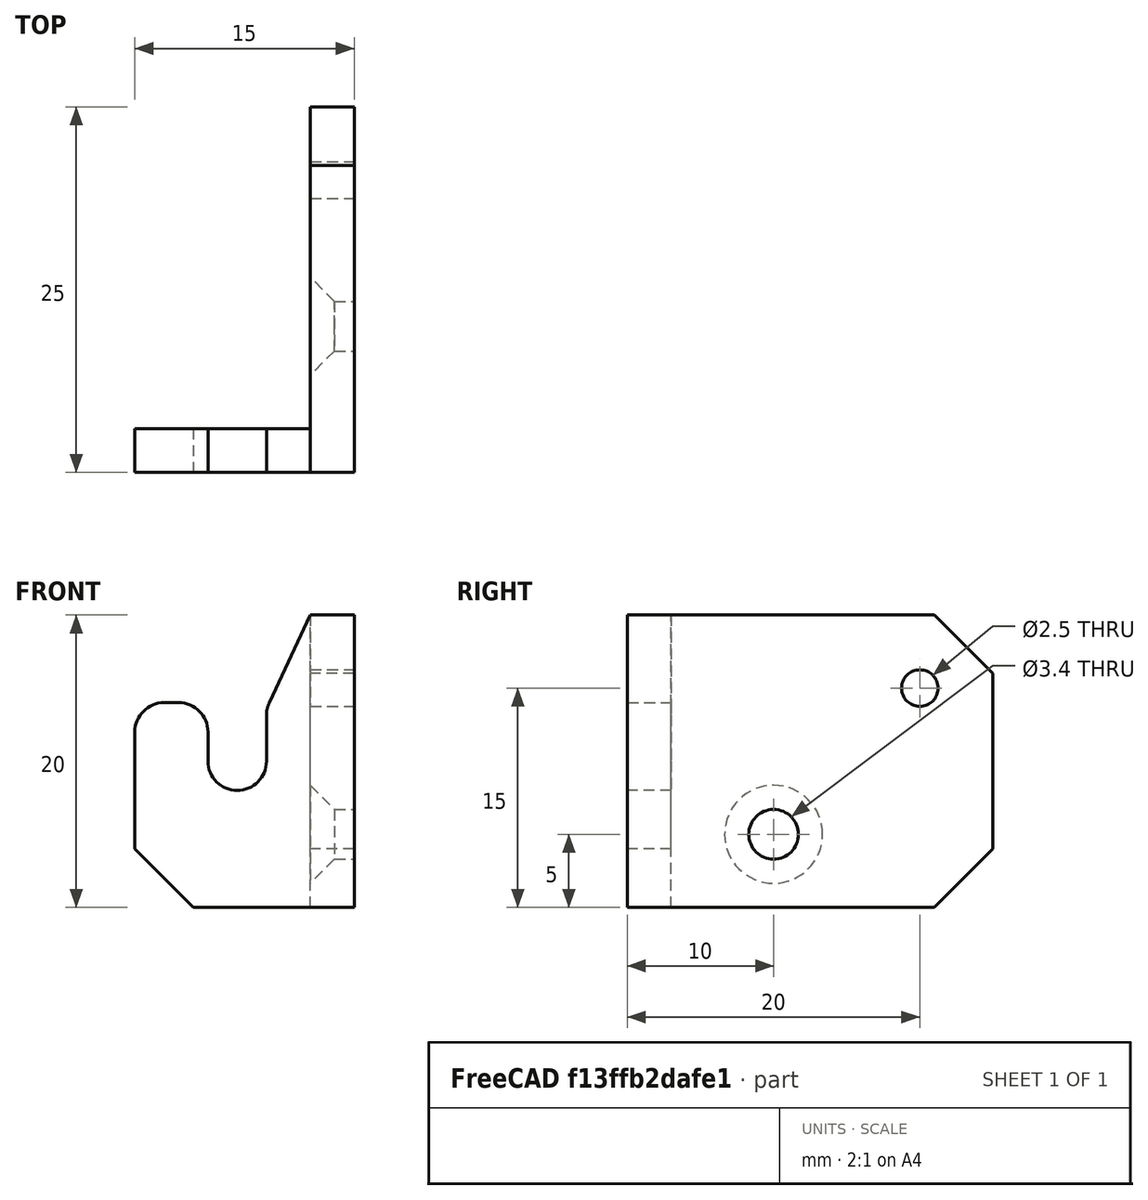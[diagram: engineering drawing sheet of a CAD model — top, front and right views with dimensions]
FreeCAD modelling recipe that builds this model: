
FCSTD DOCUMENT  (FreeCAD 0.20R28730 (Git))
Label: Tip Remover Bracket
License: All rights reserved
LicenseURL: http://en.wikipedia.org/wiki/All_rights_reserved
objects: TechDraw::DrawViewDimension×14, Sketcher::SketchObject×4, PartDesign::CoordinateSystem×4, TechDraw::DrawProjGroupItem×4, TechDraw::DrawViewBalloon×4, PartDesign::Hole×2, PartDesign::Pad×1, PartDesign::Pocket×1, PartDesign::Chamfer×1, TechDraw::DrawSVGTemplate×1, PartDesign::Body×1, TechDraw::DrawProjGroup×1, TechDraw::DrawViewAnnotation×1, TechDraw::DrawPage×1
note: 19 computed .brp shape members not serialized (recipe doc carries the construction recipe); baked Part::Feature solids carry a one-line shape summary decoded from their .brp

FEATURE [Sketcher::SketchObject] Sketch
  FullyConstrained = true
  MapMode = 5
  Support = -> [XY_Plane]
  sketch-geometry (6):
    g0: LineSegment StartX=0 StartY=0 StartZ=0 EndX=0 EndY=25 EndZ=0
    g1: LineSegment StartX=0 StartY=25 StartZ=0 EndX=-3 EndY=25 EndZ=0
    g2: LineSegment StartX=-3 StartY=25 StartZ=0 EndX=-3 EndY=3 EndZ=0
    g3: LineSegment StartX=-3 StartY=3 StartZ=0 EndX=-15 EndY=3 EndZ=0
    g4: LineSegment StartX=-15 StartY=3 StartZ=0 EndX=-15 EndY=0 EndZ=0
    g5: LineSegment StartX=-15 StartY=0 StartZ=0 EndX=0 EndY=0 EndZ=0
  constraints (17):
    c: Coincident(g-1,g0)
    c: PointOnObject(g0,g-2)
    c: Coincident(g0,g1)
    c: Horizontal(g1)
    c: Coincident(g1,g2)
    c: Vertical(g2)
    c: Coincident(g2,g3)
    c: Horizontal(g3)
    c: Coincident(g3,g4)
    c: PointOnObject(g4,g-1)
    c: Vertical(g4)
    c: Coincident(g4,g5)
    c: Coincident(g5,g0)
    c: Equal(g4,g1)
    c: DistanceY(g4,g4) = 3
    c: DistanceY(g0,g0) = 25
    c: DistanceX(g5,g5) = 15
FEATURE [PartDesign::Pad] Pad
  Direction = (0,0,1)
  Length = 20
  Length2 = 10
  Profile = -> Sketch
  ReferenceAxis = -> Sketch [N_Axis]
  Refine = true
  Type = 0
FEATURE [Sketcher::SketchObject] Sketch027
  ExternalGeometry = -> [Pad]
  FullyConstrained = true
  MapMode = 5
  Placement = pos=(0,0,0) rot=(1,0,0;1.5708rad)
  Support = -> [XZ_Plane]
  sketch-geometry (10):
    g0: LineSegment StartX=-3 StartY=20 StartZ=0 EndX=-5.81108 EndY=14 EndZ=0
    g1: LineSegment StartX=-6 StartY=13.1515 StartZ=0 EndX=-6 EndY=10 EndZ=0
    g2: ArcOfCircle CenterX=-8 CenterY=10 CenterZ=0 NormalX=0 NormalY=0 NormalZ=1 AngleXU=0 Radius=2 StartAngle=3.14159 EndAngle=6.28319
    g3: LineSegment StartX=-10 StartY=10 StartZ=0 EndX=-10 EndY=12 EndZ=0
    g4: LineSegment StartX=-15 StartY=12 StartZ=0 EndX=-15 EndY=20 EndZ=0
    g5: LineSegment StartX=-15 StartY=20 StartZ=0 EndX=-3 EndY=20 EndZ=0
    g6: ArcOfCircle CenterX=-12 CenterY=12 CenterZ=0 NormalX=0 NormalY=0 NormalZ=1 AngleXU=0 Radius=2 StartAngle=0 EndAngle=1.5708
    g7: ArcOfCircle CenterX=-4 CenterY=13.1515 CenterZ=0 NormalX=0 NormalY=0 NormalZ=1 AngleXU=0 Radius=2 StartAngle=2.70345 EndAngle=3.14159
    g8: LineSegment StartX=-12 StartY=14 StartZ=0 EndX=-13 EndY=14 EndZ=0
    g9: ArcOfCircle CenterX=-13 CenterY=12 CenterZ=0 NormalX=0 NormalY=0 NormalZ=1 AngleXU=0 Radius=2 StartAngle=1.5708 EndAngle=3.14159
  constraints (25):
    c: Coincident(g-3,g0)
    c: Vertical(g1)
    c: Tangent(g1,g2) = 1.5708
    c: Tangent(g2,g3) = 1.5708
    c: Coincident(g4,g-3)
    c: Vertical(g4)
    c: Coincident(g4,g5)
    c: Coincident(g5,g0)
    c: Vertical(g3)
    c: Radius(g2) = 2
    c: DistanceY(g-1,g2) = 10
    c: Tangent(g3,g6) = -1.5708
    c: Tangent(g0,g7) = -1.5708
    c: Tangent(g1,g7) = -1.5708
    c: Horizontal(g8)
    c: Tangent(g8,g9) = -1.5708
    c: Coincident(g4,g9)
    c: Horizontal(g4,g9)
    c: Tangent(g6,g8) = -1.5708
    c: Equal(g9,g6)
    c: Equal(g6,g7)
    c: Radius(g6) = 2
    c: DistanceX(g2,g-1) = 8
    c: DistanceY(g2,g8) = 4
    c: Horizontal(g6,g0)
FEATURE [PartDesign::Pocket] Pocket
  BaseFeature = -> Pad
  Direction = (0,1,2e-16)
  Length = 5
  Length2 = 5
  Profile = -> Sketch027
  ReferenceAxis = -> Sketch027 [N_Axis]
  Refine = true
  Type = 1
FEATURE [Sketcher::SketchObject] Sketch029
  AttachmentOffset = pos=(0,0,-3) rot=(0,0,1;0rad)
  FullyConstrained = true
  MapMode = 5
  Placement = pos=(-3,7e-16,-7e-16) rot=(0.57735,0.57735,0.57735;2.0944rad)
  Support = -> [YZ_Plane]
  expr: Constraints[1] = Sketch028.Constraints[1]
  expr: Constraints[2] = Sketch028.Constraints[2]
  expr: Constraints[3] = Sketch028.Constraints[3]
  expr: Constraints[4] = Sketch028.Constraints[4]
  expr: Constraints[5] = Sketch028.Constraints[5]
  sketch-geometry (2):
    g0: Circle CenterX=20 CenterY=15 CenterZ=0 NormalX=0 NormalY=0 NormalZ=1 AngleXU=0 Radius=1.5
    g1: Circle CenterX=10 CenterY=5 CenterZ=0 NormalX=0 NormalY=0 NormalZ=1 AngleXU=0 Radius=1.5
  constraints (6):
    c: Equal(g1,g0)
    c: Diameter(g0) = 3
    c: DistanceY(g1,g0) = 10
    c: DistanceX(g1,g0) = 10
    c: DistanceX(g-1,g0) = 20
    c: DistanceY(g-1,g0) = 15
FEATURE [Sketcher::SketchObject] Sketch028
  AttachmentOffset = pos=(0,0,-3) rot=(0,0,1;0rad)
  FullyConstrained = true
  MapMode = 5
  Placement = pos=(-3,7e-16,-7e-16) rot=(0.57735,0.57735,0.57735;2.0944rad)
  Support = -> [YZ_Plane]
  sketch-geometry (2):
    g0: Circle CenterX=20 CenterY=15 CenterZ=0 NormalX=0 NormalY=0 NormalZ=1 AngleXU=0 Radius=1.5
    g1: Circle CenterX=10 CenterY=5 CenterZ=0 NormalX=0 NormalY=0 NormalZ=1 AngleXU=0 Radius=1.5
  constraints (6):
    c: Equal(g1,g0)
    c: Diameter(g0) = 3
    c: DistanceY(g1,g0) = 10
    c: DistanceX(g1,g0) = 10
    c: DistanceX(g-1,g0) = 20
    c: DistanceY(g-1,g0) = 15
FEATURE [PartDesign::Hole] Hole
  BaseFeature = -> Pocket
  CustomThreadClearance = 0
  Depth = 25
  DepthType = 0
  Diameter = 3.4
  DrillForDepth = false
  DrillPoint = 1
  DrillPointAngle = 118
  HoleCutCountersinkAngle = 90
  HoleCutCustomValues = false
  HoleCutDepth = 2.8
  HoleCutDiameter = 6.7
  HoleCutType = 7
  ModelThread = false
  Profile = -> Sketch028
  Refine = true
  Reversed = true
  Tapered = false
  TaperedAngle = 90
  ThreadClass = 0
  ThreadDepth = 25
  ThreadDepthType = 0
  ThreadDirection = 0
  ThreadFit = 0
  ThreadSize = 9
  ThreadType = 1
  Threaded = false
  UseCustomThreadClearance = false
FEATURE [PartDesign::Hole] Hole002
  BaseFeature = -> Hole
  CustomThreadClearance = 0
  Depth = 87.4919
  DepthType = 1
  Diameter = 2.5
  DrillForDepth = false
  DrillPoint = 1
  DrillPointAngle = 118
  HoleCutCountersinkAngle = 90
  HoleCutCustomValues = false
  HoleCutDepth = 0
  HoleCutDiameter = 6.1
  HoleCutType = 0
  ModelThread = false
  Profile = -> Sketch029
  Refine = true
  Reversed = true
  Tapered = false
  TaperedAngle = 90
  ThreadClass = 0
  ThreadDepth = 87.4919
  ThreadDepthType = 0
  ThreadDirection = 0
  ThreadFit = 0
  ThreadSize = 9
  ThreadType = 1
  Threaded = true
  UseCustomThreadClearance = false
FEATURE [PartDesign::Chamfer] Chamfer003
  Angle = 45
  Base = -> Hole002 [Edge21,Edge18,Edge24]
  BaseFeature = -> Hole002
  ChamferType = 0
  FlipDirection = false
  Refine = true
  Size = 4
  Size2 = 1
  SupportTransform = false
  UseAllEdges = false
FEATURE [PartDesign::CoordinateSystem] Hole1001  label="LCS_Tip_Remover_Bracket_Hole_1_Inside"
  AttacherType = Attacher::AttachEngine3D
  AttachmentOffset = pos=(0,0,0) rot=(0,0,-1;1.5708rad)
  MapMode = 11
  Placement = pos=(0,20,15) rot=(-0.707107,0,-0.707107;3.14159rad)
  Support = -> [Chamfer003]
FEATURE [TechDraw::DrawSVGTemplate] Template
  EditableTexts = AUTHOR_NAME=Håvard Jakobsen; DN=-; DRAWING_TITLE=Tip Remover Bracket Drawing; FC-DATE=20220501; FC-REV=REV 1; FC-SC=3:1; FC-SH=1/1; FC-SI=A3; FreeCAD_DRAWING=Tolerances according to ISO 2768-1: c (Coarse); PN=-; SI-1=Tip Remover Bracket for OpenSolder Stand; SI-2=Material: EN AW 6082 T6; SI-5=https://github.com/<owner>/OpenSolder; SI-6=Licence: GPL-3.0
  Height = 297
  Orientation = 1
  Width = 420
FEATURE [PartDesign::CoordinateSystem] LCS_Tip_Remover_Bracket_Hole_1_Outside
  AttacherType = Attacher::AttachEngine3D
  MapMode = 11
  Placement = pos=(-3,20,15) rot=(0.57735,0.57735,-0.57735;4.18879rad)
  Support = -> [Chamfer003]
FEATURE [PartDesign::CoordinateSystem] LCS_Tip_Remover_Bracket_Hole_2_Outside
  AttacherType = Attacher::AttachEngine3D
  MapMode = 11
  Placement = pos=(-3,10,5) rot=(0.57735,0.57735,-0.57735;4.18879rad)
  Support = -> [Chamfer003]
FEATURE [PartDesign::CoordinateSystem] LCS_Tip_Remover_Bracket_Tip_Attachment
  AttacherType = Attacher::AttachEngine3D
  MapMode = 11
  Placement = pos=(-8,3,10) rot=(0.57735,0.57735,-0.57735;2.0944rad)
  Support = -> [Chamfer003]
FEATURE [PartDesign::Body] Body  label="Tip_Remover_Bracket"
  Group = -> [Sketch,Pad,Sketch027,Pocket,Sketch028,Sketch029,Hole,Hole002,Chamfer003,Hole1001,LCS_Tip_Remover_Bracket_Hole_1_Outside,LCS_Tip_Remover_Bracket_Hole_2_Outside,LCS_Tip_Remover_Bracket_Tip_Attachment]
  Origin = -> Origin
  Tip = -> Chamfer003
FEATURE [TechDraw::DrawProjGroupItem] ProjItem  label="Front"
  CoarseView = false
  Direction = (-1,0,0)
  Focus = 100
  HardHidden = false
  IsoCount = 0
  IsoHidden = false
  IsoVisible = false
  LockPosition = true
  Perspective = false
  Rotation = 0
  RotationVector = (0,-1,0)
  Scale = 3
  ScaleType = 2
  SeamHidden = false
  SeamVisible = true
  SmoothHidden = false
  SmoothVisible = true
  Source = -> [Body]
  Type = 0
  X = 0
  XDirection = (0,-1,0)
  Y = 0
FEATURE [TechDraw::DrawProjGroupItem] ProjItem002  label="Bottom"
  CoarseView = false
  Direction = (0,0,-1)
  Focus = 100
  HardHidden = false
  IsoCount = 0
  IsoHidden = false
  IsoVisible = false
  LockPosition = false
  Perspective = false
  Rotation = 0
  RotationVector = (1,0,0)
  Scale = 3
  ScaleType = 2
  SeamHidden = false
  SeamVisible = true
  SmoothHidden = false
  SmoothVisible = true
  Source = -> [Body]
  Type = 5
  X = 0
  XDirection = (0,-1,0)
  Y = 96.5908
FEATURE [TechDraw::DrawProjGroupItem] ProjItem003  label="FrontTopRight"
  CoarseView = false
  Direction = (-0.57735,-0.57735,0.57735)
  Focus = 100
  HardHidden = false
  IsoCount = 0
  IsoHidden = false
  IsoVisible = false
  LockPosition = true
  Perspective = false
  Rotation = 0
  RotationVector = (1,0,0)
  Scale = 3
  ScaleType = 2
  SeamHidden = false
  SeamVisible = true
  SmoothHidden = false
  SmoothVisible = true
  Source = -> [Body]
  Type = 7
  X = -211.449
  XDirection = (0.707107,-0.707107,0)
  Y = -71.1703
FEATURE [TechDraw::DrawViewDimension] Dimension
  AngleOverride = false
  Arbitrary = false
  ArbitraryTolerances = false
  EqualTolerance = true
  ExtensionAngle = 0
  FormatSpec = %.2f
  FormatSpecOverTolerance = %+.2f
  FormatSpecUnderTolerance = %+.2f
  Inverted = false
  LineAngle = 0
  LockPosition = false
  MeasureType = 1
  OverTolerance = 0
  References2D = -> [ProjItem002]
  Rotation = 0
  ScaleType = 1
  TheoreticalExact = false
  Type = 2
  UnderTolerance = 0
  X = 45
  Y = 2
FEATURE [TechDraw::DrawViewDimension] Dimension001
  AngleOverride = false
  Arbitrary = false
  ArbitraryTolerances = false
  EqualTolerance = true
  ExtensionAngle = 0
  FormatSpec = %.2f
  FormatSpecOverTolerance = %+.2f
  FormatSpecUnderTolerance = %+.2f
  Inverted = false
  LineAngle = 0
  LockPosition = false
  MeasureType = 1
  OverTolerance = 0
  References2D = -> [ProjItem002]
  Rotation = 0
  ScaleType = 1
  TheoreticalExact = false
  Type = 1
  UnderTolerance = 0
  X = 0
  Y = -27
FEATURE [TechDraw::DrawViewDimension] Dimension002
  AngleOverride = false
  Arbitrary = false
  ArbitraryTolerances = false
  EqualTolerance = true
  ExtensionAngle = 0
  FormatSpec = %.2f
  FormatSpecOverTolerance = %+.2f
  FormatSpecUnderTolerance = %+.2f
  Inverted = false
  LineAngle = 0
  LockPosition = false
  MeasureType = 1
  OverTolerance = 0
  References2D = -> [ProjItem002]
  Rotation = 0
  ScaleType = 1
  TheoreticalExact = false
  Type = 1
  UnderTolerance = 0
  X = 33
  Y = 38
FEATURE [TechDraw::DrawViewDimension] Dimension004
  AngleOverride = false
  Arbitrary = false
  ArbitraryTolerances = false
  EqualTolerance = true
  ExtensionAngle = 0
  FormatSpec = %.2f
  FormatSpecOverTolerance = %+.2f
  FormatSpecUnderTolerance = %+.2f
  Inverted = false
  LineAngle = 0
  LockPosition = false
  MeasureType = 1
  OverTolerance = 0
  References2D = -> [ProjItem]
  Rotation = 0
  ScaleType = 1
  TheoreticalExact = false
  Type = 1
  UnderTolerance = 0
  X = 22
  Y = -36
FEATURE [TechDraw::DrawViewDimension] Dimension005
  AngleOverride = false
  Arbitrary = false
  ArbitraryTolerances = false
  EqualTolerance = true
  ExtensionAngle = 0
  FormatSpec = %.2f
  FormatSpecOverTolerance = %+.2f
  FormatSpecUnderTolerance = %+.2f
  Inverted = false
  LineAngle = 0
  LockPosition = false
  MeasureType = 1
  OverTolerance = 0
  References2D = -> [ProjItem]
  Rotation = 0
  ScaleType = 1
  TheoreticalExact = false
  Type = 1
  UnderTolerance = 0
  X = 8
  Y = -46
FEATURE [TechDraw::DrawViewDimension] Dimension006
  AngleOverride = false
  Arbitrary = false
  ArbitraryTolerances = false
  EqualTolerance = true
  ExtensionAngle = 0
  FormatSpec = %.2f
  FormatSpecOverTolerance = %+.2f
  FormatSpecUnderTolerance = %+.2f
  Inverted = false
  LineAngle = 0
  LockPosition = false
  MeasureType = 1
  OverTolerance = 0
  References2D = -> [ProjItem]
  Rotation = 0
  ScaleType = 1
  TheoreticalExact = false
  Type = 2
  UnderTolerance = 0
  X = 47
  Y = 0
FEATURE [TechDraw::DrawViewDimension] Dimension007
  AngleOverride = false
  Arbitrary = false
  ArbitraryTolerances = false
  EqualTolerance = true
  ExtensionAngle = 0
  FormatSpec = %.2f
  FormatSpecOverTolerance = %+.2f
  FormatSpecUnderTolerance = %+.2f
  Inverted = false
  LineAngle = 0
  LockPosition = false
  MeasureType = 1
  OverTolerance = 0
  References2D = -> [ProjItem]
  Rotation = 0
  ScaleType = 1
  TheoreticalExact = false
  Type = 2
  UnderTolerance = 0
  X = 57
  Y = -6
FEATURE [TechDraw::DrawViewBalloon] Balloon
  BubbleShape = 7
  EndType = 0
  EndTypeScale = 1
  KinkLength = 5
  LockPosition = false
  OriginX = -10.5
  OriginY = 8
  Rotation = 0
  ScaleType = 1
  ShapeScale = 1
  SourceView = -> ProjItem
  Text = 2x 4 X 45°
  TextWrapLen = -1
  X = -21.8707
  Y = 15.2351
FEATURE [TechDraw::DrawViewBalloon] Balloon001
  BubbleShape = 7
  EndType = 0
  EndTypeScale = 1
  KinkLength = 5
  LockPosition = false
  OriginX = 5
  OriginY = -3
  Rotation = 0
  ScaleType = 1
  ShapeScale = 1
  SourceView = -> ProjItem
  Text = ⌀3.4 THRU ⌵ 6.7 x 45°
  TextWrapLen = -1
  X = 28.452
  Y = 11.5839
FEATURE [TechDraw::DrawProjGroupItem] ProjItem001  label="Right"
  CoarseView = false
  Direction = (-1e-16,-1,0)
  Focus = 100
  HardHidden = true
  IsoCount = 0
  IsoHidden = false
  IsoVisible = false
  LockPosition = false
  Perspective = false
  Rotation = 0
  RotationVector = (1,0,0)
  Scale = 3
  ScaleType = 2
  SeamHidden = false
  SeamVisible = true
  SmoothHidden = false
  SmoothVisible = true
  Source = -> [Body]
  Type = 2
  X = -106.591
  XDirection = (1,-1e-16,0)
  Y = 0
FEATURE [TechDraw::DrawProjGroup] ProjGroup
  Anchor = -> ProjItem
  AutoDistribute = true
  LockPosition = true
  ProjectionType = 0
  Rotation = 0
  Scale = 3
  ScaleType = 0
  Source = -> [Body]
  Views = -> [ProjItem,ProjItem001,ProjItem002,ProjItem003]
  X = 280
  Y = 140
  spacingX = 40
  spacingY = 30
FEATURE [TechDraw::DrawViewDimension] Dimension015
  AngleOverride = false
  Arbitrary = false
  ArbitraryTolerances = false
  EqualTolerance = true
  ExtensionAngle = 0
  FormatSpec = 3x R%.2f
  FormatSpecOverTolerance = %+.2f
  FormatSpecUnderTolerance = %+.2f
  Inverted = false
  LineAngle = 0
  LockPosition = false
  MeasureType = 1
  OverTolerance = 0
  References2D = -> [ProjItem001]
  Rotation = 0
  ScaleType = 1
  TheoreticalExact = false
  Type = 4
  UnderTolerance = 0
  X = -36.8234
  Y = 31.4867
FEATURE [TechDraw::DrawViewDimension] Dimension014
  AngleOverride = false
  Arbitrary = false
  ArbitraryTolerances = false
  EqualTolerance = true
  ExtensionAngle = 0
  FormatSpec = %.2f
  FormatSpecOverTolerance = %+.2f
  FormatSpecUnderTolerance = %+.2f
  Inverted = false
  LineAngle = 0
  LockPosition = false
  MeasureType = 1
  OverTolerance = 0
  References2D = -> [ProjItem001]
  Rotation = 0
  ScaleType = 1
  TheoreticalExact = false
  Type = 1
  UnderTolerance = 0
  X = 6
  Y = -45
FEATURE [TechDraw::DrawViewDimension] Dimension012
  AngleOverride = false
  Arbitrary = false
  ArbitraryTolerances = false
  EqualTolerance = true
  ExtensionAngle = 0
  FormatSpec = R%.2f
  FormatSpecOverTolerance = %+.2f
  FormatSpecUnderTolerance = %+.2f
  Inverted = false
  LineAngle = 0
  LockPosition = false
  MeasureType = 1
  OverTolerance = 0
  References2D = -> [ProjItem001]
  Rotation = 0
  ScaleType = 1
  TheoreticalExact = false
  Type = 4
  UnderTolerance = 0
  X = -14.5426
  Y = -9.1845
FEATURE [TechDraw::DrawViewDimension] Dimension010
  AngleOverride = false
  Arbitrary = false
  ArbitraryTolerances = false
  EqualTolerance = true
  ExtensionAngle = 0
  FormatSpec = %.2f
  FormatSpecOverTolerance = %+.2f
  FormatSpecUnderTolerance = %+.2f
  Inverted = false
  LineAngle = 0
  LockPosition = false
  MeasureType = 1
  OverTolerance = 0
  References2D = -> [ProjItem001]
  Rotation = 0
  ScaleType = 1
  TheoreticalExact = false
  Type = 2
  UnderTolerance = 0
  X = -46
  Y = -6
FEATURE [TechDraw::DrawViewDimension] Dimension003
  AngleOverride = false
  Arbitrary = false
  ArbitraryTolerances = false
  EqualTolerance = true
  ExtensionAngle = 0
  FormatSpec = %.2f
  FormatSpecOverTolerance = %+.2f
  FormatSpecUnderTolerance = %+.2f
  Inverted = false
  LineAngle = 0
  LockPosition = false
  MeasureType = 1
  OverTolerance = 0
  References2D = -> [ProjItem001]
  Rotation = 0
  ScaleType = 1
  TheoreticalExact = false
  Type = 2
  UnderTolerance = 0
  X = 30
  Y = 1
FEATURE [TechDraw::DrawViewDimension] Dimension009
  AngleOverride = false
  Arbitrary = false
  ArbitraryTolerances = false
  EqualTolerance = true
  ExtensionAngle = 0
  FormatSpec = %.2f
  FormatSpecOverTolerance = %+.2f
  FormatSpecUnderTolerance = %+.2f
  Inverted = false
  LineAngle = 0
  LockPosition = false
  MeasureType = 1
  OverTolerance = 0
  References2D = -> [ProjItem001]
  Rotation = 0
  ScaleType = 1
  TheoreticalExact = false
  Type = 2
  UnderTolerance = 0
  X = -36
  Y = -12
FEATURE [TechDraw::DrawViewDimension] Dimension013
  AngleOverride = false
  Arbitrary = false
  ArbitraryTolerances = false
  EqualTolerance = true
  ExtensionAngle = 0
  FormatSpec = %.2f
  FormatSpecOverTolerance = %+.2f
  FormatSpecUnderTolerance = %+.2f
  Inverted = false
  LineAngle = 0
  LockPosition = false
  MeasureType = 1
  OverTolerance = 0
  References2D = -> [ProjItem001]
  Rotation = 0
  ScaleType = 1
  TheoreticalExact = false
  Type = 1
  UnderTolerance = 0
  X = 10
  Y = -35
FEATURE [TechDraw::DrawViewBalloon] Balloon002
  BubbleShape = 7
  EndType = 0
  EndTypeScale = 1
  KinkLength = 5
  LockPosition = false
  OriginX = -5.54447
  OriginY = -8
  Rotation = 0
  ScaleType = 1
  ShapeScale = 1
  SourceView = -> ProjItem001
  Text = 4 X 45°
  TextWrapLen = -1
  X = -16.2666
  Y = -13.0297
FEATURE [TechDraw::DrawViewBalloon] Balloon003
  BubbleShape = 7
  EndType = 0
  EndTypeScale = 1
  KinkLength = 5
  LockPosition = false
  OriginX = -6.5
  OriginY = 5.75
  Rotation = 0
  ScaleType = 1
  ShapeScale = 1
  SourceView = -> ProjItem
  Text = M3x0.5 - 6H THRU
  TextWrapLen = -1
  X = 10.3006
  Y = 16.6674
FEATURE [TechDraw::DrawViewAnnotation] Annotation
  Font = osifont
  LineSpace = 80
  LockPosition = false
  MaxWidth = -1
  Rotation = 0
  ScaleType = 1
  Text = DIY manufacturing tips: | - Use an aluminium angle, 2-5mm thick | - Drill the two mounting holes, then the tip remover hole (Ø4) | - Mark and cut the shape roughly using a hacksaw | - File all edges smooth
  TextSize = 4
  TextStyle = 0
  X = 79.449
  Y = 268.383
FEATURE [TechDraw::DrawPage] Page
  KeepUpdated = true
  NextBalloonIndex = 5
  ProjectionType = 0
  Scale = 3
  Template = -> Template
  Views = -> [ProjGroup,Dimension,Dimension001,Dimension002,Dimension003,Dimension004,Dimension005,Dimension006,Dimension007,Balloon,Balloon001,Dimension009,Dimension010,Dimension012,Dimension013,Dimension014,Balloon002,Dimension015,Balloon003,Annotation]
